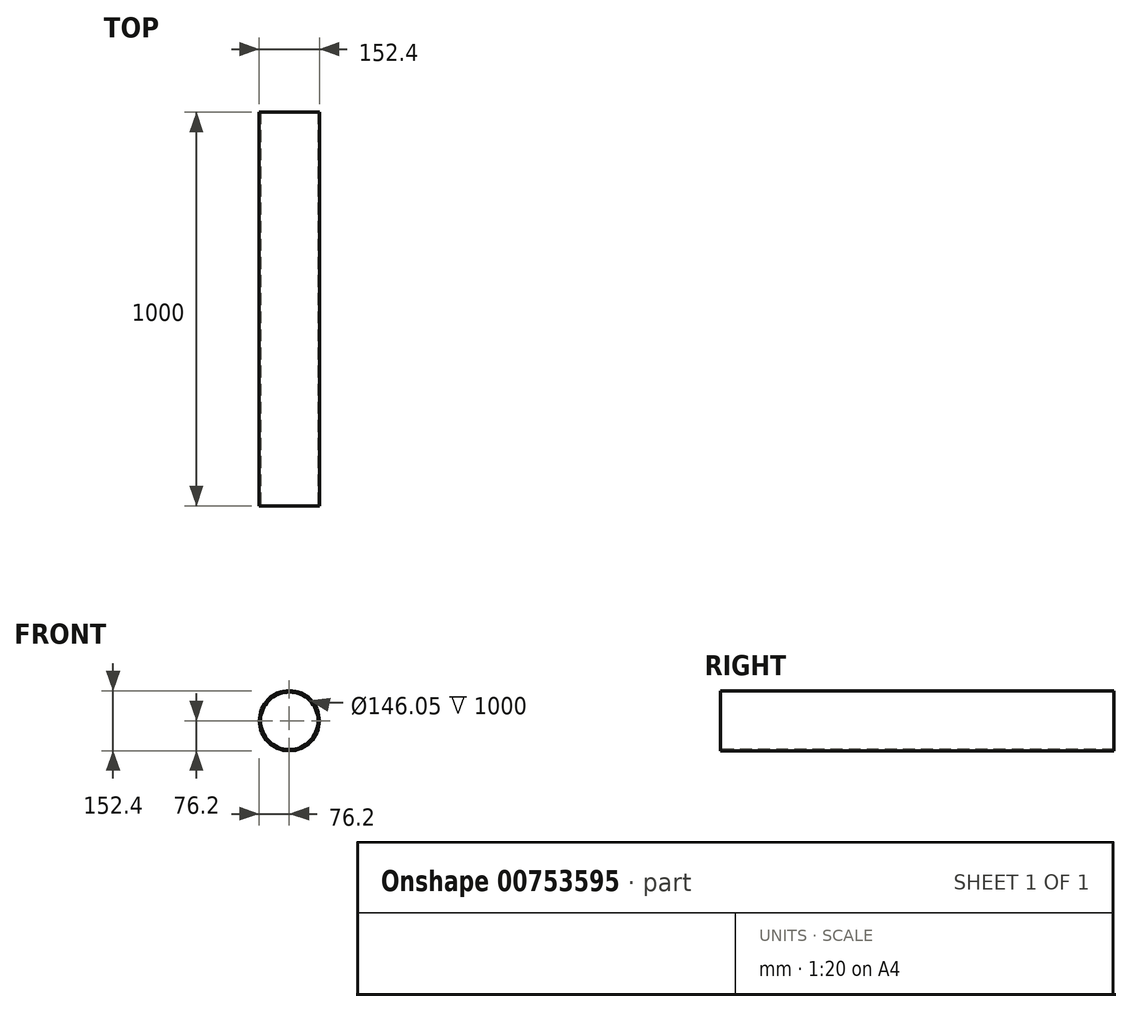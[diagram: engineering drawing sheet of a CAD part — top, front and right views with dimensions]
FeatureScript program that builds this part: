
annotation { "Feature Type Name" : "Feature", "Feature Type Description" : "" }
export const myFeature = defineFeature(function(context is Context, id is Id, definition is map)
    precondition{}
    {
        {
            var Q0;
            Q0=qCreatedBy(makeId("Front.planeOp"),FACE);
            var sketch = newSketch(context, id + "F0", { "sketchPlane" : qUnion([Q0])});
            skCircle(sketch, "E0", {"center": v(0, 0) * mm, "radius": 76.2 * mm});
            skCircle(sketch, "E1.0", {"center": v(0, 0) * mm, "radius": 73.03 * mm});
            skSolve(sketch);
        }
        {
            var Q0;
            Q0 = qSketchRegion(id + "F0", true);
            extrude(context, id + "F1", {"entities" : qUnion([Q0]), "oppositeDirection" : true, "depth" : 1000 * mm, "offsetDistance" : 25 * mm});
        }
    });
